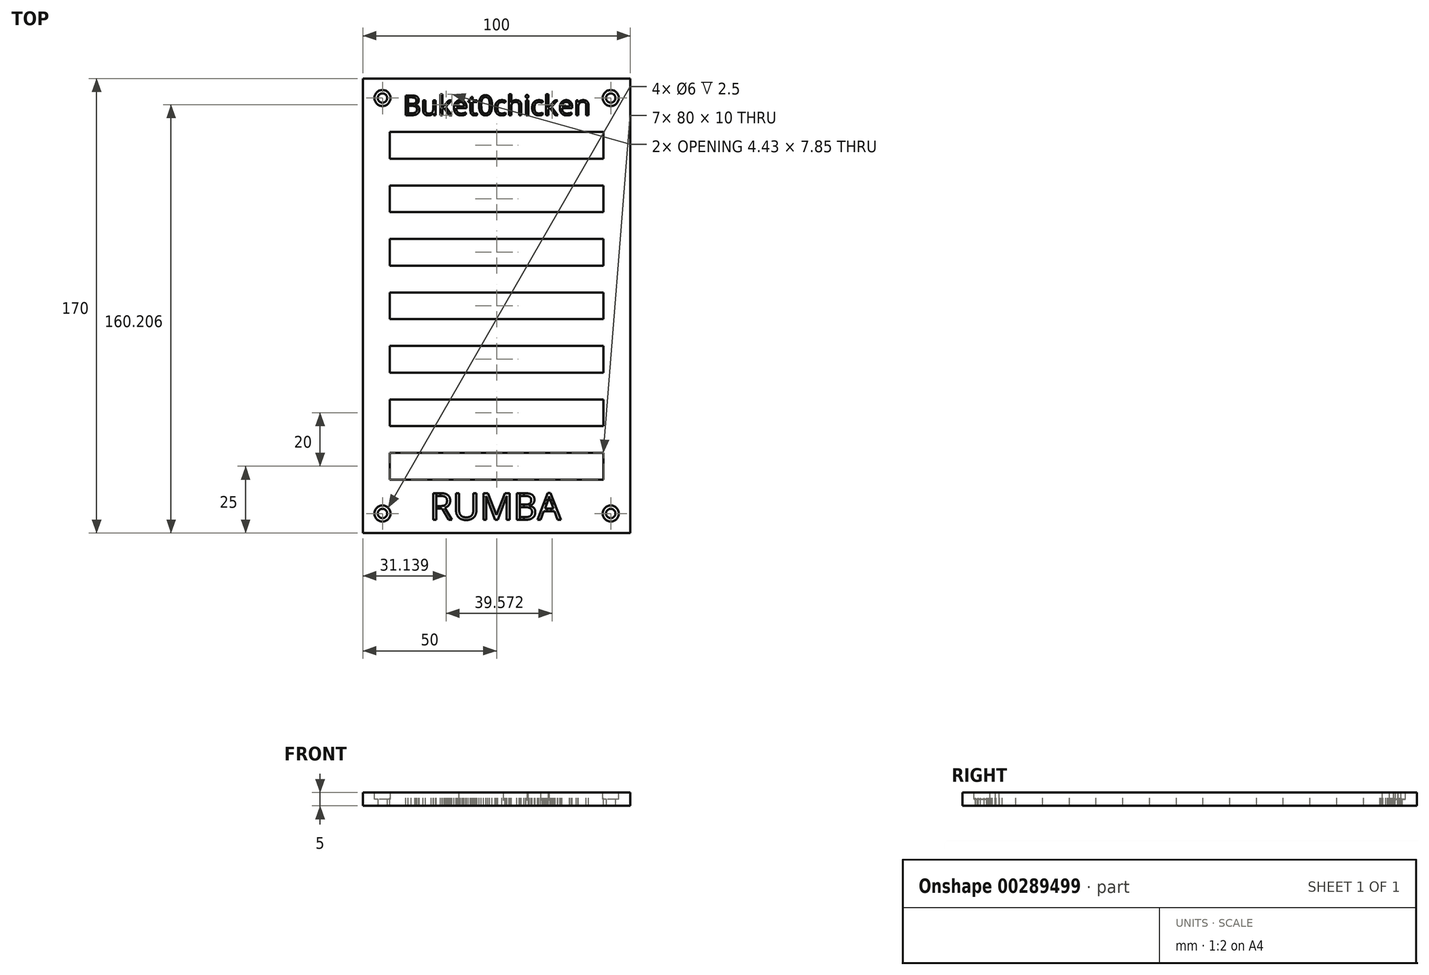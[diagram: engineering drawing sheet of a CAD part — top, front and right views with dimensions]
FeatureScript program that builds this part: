
annotation { "Feature Type Name" : "Feature", "Feature Type Description" : "" }
export const myFeature = defineFeature(function(context is Context, id is Id, definition is map)
    precondition{}
    {
        {
            var Q0;
            Q0=qCreatedBy(makeId("Top.planeOp"),FACE);
            var sketch = newSketch(context, id + "F0", { "sketchPlane" : qUnion([Q0])});
            skLineSegment(sketch, "E0.bottom", {"start": v(0, 0) * mm, "end": v(100, 0) * mm});
            skLineSegment(sketch, "E0.top", {"start": v(0, 170) * mm, "end": v(100, 170) * mm});
            skLineSegment(sketch, "E0.left", {"start": v(0, 0) * mm, "end": v(0, 170) * mm});
            skLineSegment(sketch, "E0.right", {"start": v(100, 0) * mm, "end": v(100, 170) * mm});
            skCircle(sketch, "E1", {"center": v(7.32, 162.68) * mm, "radius": 1.75 * mm});
            skCircle(sketch, "E2", {"center": v(92.68, 162.68) * mm, "radius": 1.75 * mm});
            skCircle(sketch, "E3", {"center": v(7.32, 7.32) * mm, "radius": 1.75 * mm});
            skCircle(sketch, "E4", {"center": v(92.68, 7.32) * mm, "radius": 1.75 * mm});
            skSolve(sketch);
        }
        {
            var Q0;
            Q0 = qSketchRegion(id + "F0", true);
            extrude(context, id + "F1", {"entities" : qUnion([Q0]), "depth" : 5 * mm});
        }
        {
            var Q0;
            Q0=makeQuery(id+"F1.opExtrude","CAP_FACE",FACE,{"disambiguationData":[OSD([sQuery(id+"F0.wireOp",EDGE,"E0.bottom"),sQuery(id+"F0.wireOp",EDGE,"E0.top"),sQuery(id+"F0.wireOp",EDGE,"E0.left"),sQuery(id+"F0.wireOp",EDGE,"E0.right"),sQuery(id+"F0.wireOp",EDGE,"E1"),sQuery(id+"F0.wireOp",EDGE,"E2"),sQuery(id+"F0.wireOp",EDGE,"E3"),sQuery(id+"F0.wireOp",EDGE,"E4")])],"isStart":false});
            var sketch = newSketch(context, id + "F2", { "sketchPlane" : qUnion([Q0])});
            skCircle(sketch, "E5.0", {"center": v(7.32, 162.68) * mm, "radius": 1.75 * mm, "construction": true});
            skCircle(sketch, "E6.0", {"center": v(92.68, 162.68) * mm, "radius": 1.75 * mm, "construction": true});
            skCircle(sketch, "E7.0", {"center": v(92.68, 7.32) * mm, "radius": 1.75 * mm, "construction": true});
            skCircle(sketch, "E8.0", {"center": v(7.32, 7.32) * mm, "radius": 1.75 * mm, "construction": true});
            skCircle(sketch, "E9", {"center": v(7.32, 162.68) * mm, "radius": 3 * mm});
            skCircle(sketch, "E10", {"center": v(92.68, 162.68) * mm, "radius": 3 * mm});
            skCircle(sketch, "E11", {"center": v(7.32, 7.32) * mm, "radius": 3 * mm});
            skCircle(sketch, "E12", {"center": v(92.68, 7.32) * mm, "radius": 3 * mm});
            skSolve(sketch);
        }
        {
            var Q0;
            Q0 = qSketchRegion(id + "F2", true);
            extrude(context, id + "F3", {"entities" : qUnion([Q0]), "operationType" : NewBodyOperationType.REMOVE, "oppositeDirection" : true, "depth" : 2.5 * mm});
        }
        {
            var Q0;
            Q0=makeQuery(id+"F1.opExtrude","CAP_FACE",FACE,{"disambiguationData":[OSD([sQuery(id+"F0.wireOp",EDGE,"E0.bottom"),sQuery(id+"F0.wireOp",EDGE,"E0.top"),sQuery(id+"F0.wireOp",EDGE,"E0.left"),sQuery(id+"F0.wireOp",EDGE,"E0.right"),sQuery(id+"F0.wireOp",EDGE,"E1"),sQuery(id+"F0.wireOp",EDGE,"E2"),sQuery(id+"F0.wireOp",EDGE,"E3"),sQuery(id+"F0.wireOp",EDGE,"E4")])],"isStart":false});
            var sketch = newSketch(context, id + "F4", { "sketchPlane" : qUnion([Q0])});
            skLineSegment(sketch, "E13.0.0", {"start": v(100, 170) * mm, "end": v(0, 170) * mm, "construction": true});
            skLineSegment(sketch, "E13.0.1", {"start": v(0, 170) * mm, "end": v(0, 0) * mm, "construction": true});
            skLineSegment(sketch, "E13.0.2", {"start": v(0, 0) * mm, "end": v(100, 0) * mm, "construction": true});
            skLineSegment(sketch, "E13.0.3", {"start": v(100, 0) * mm, "end": v(100, 170) * mm, "construction": true});
            skLineSegment(sketch, "E14.bottom", {"start": v(10, 150) * mm, "end": v(90, 150) * mm});
            skLineSegment(sketch, "E14.top", {"start": v(10, 140) * mm, "end": v(90, 140) * mm});
            skLineSegment(sketch, "E14.left", {"start": v(10, 150) * mm, "end": v(10, 140) * mm});
            skLineSegment(sketch, "E14.right", {"start": v(90, 150) * mm, "end": v(90, 140) * mm});
            skLineSegment(sketch, "E15.0.1.0", {"start": v(90, 130) * mm, "end": v(90, 120) * mm});
            skLineSegment(sketch, "E15.0.1.1", {"start": v(10, 130) * mm, "end": v(90, 130) * mm});
            skLineSegment(sketch, "E15.0.1.2", {"start": v(10, 120) * mm, "end": v(90, 120) * mm});
            skLineSegment(sketch, "E15.0.1.3", {"start": v(10, 130) * mm, "end": v(10, 120) * mm});
            skLineSegment(sketch, "E15.0.2.0", {"start": v(90, 110) * mm, "end": v(90, 100) * mm});
            skLineSegment(sketch, "E15.0.2.1", {"start": v(10, 110) * mm, "end": v(90, 110) * mm});
            skLineSegment(sketch, "E15.0.2.2", {"start": v(10, 100) * mm, "end": v(90, 100) * mm});
            skLineSegment(sketch, "E15.0.2.3", {"start": v(10, 110) * mm, "end": v(10, 100) * mm});
            skLineSegment(sketch, "E15.0.3.0", {"start": v(90, 90) * mm, "end": v(90, 80) * mm});
            skLineSegment(sketch, "E15.0.3.1", {"start": v(10, 90) * mm, "end": v(90, 90) * mm});
            skLineSegment(sketch, "E15.0.3.2", {"start": v(10, 80) * mm, "end": v(90, 80) * mm});
            skLineSegment(sketch, "E15.0.3.3", {"start": v(10, 90) * mm, "end": v(10, 80) * mm});
            skLineSegment(sketch, "E15.0.4.0", {"start": v(90, 70) * mm, "end": v(90, 60) * mm});
            skLineSegment(sketch, "E15.0.4.1", {"start": v(10, 70) * mm, "end": v(90, 70) * mm});
            skLineSegment(sketch, "E15.0.4.2", {"start": v(10, 60) * mm, "end": v(90, 60) * mm});
            skLineSegment(sketch, "E15.0.4.3", {"start": v(10, 70) * mm, "end": v(10, 60) * mm});
            skLineSegment(sketch, "E15.0.5.0", {"start": v(90, 50) * mm, "end": v(90, 40) * mm});
            skLineSegment(sketch, "E15.0.5.1", {"start": v(10, 50) * mm, "end": v(90, 50) * mm});
            skLineSegment(sketch, "E15.0.5.2", {"start": v(10, 40) * mm, "end": v(90, 40) * mm});
            skLineSegment(sketch, "E15.0.5.3", {"start": v(10, 50) * mm, "end": v(10, 40) * mm});
            skLineSegment(sketch, "E15.0.6.0", {"start": v(90, 30) * mm, "end": v(90, 20) * mm});
            skLineSegment(sketch, "E15.0.6.1", {"start": v(10, 30) * mm, "end": v(90, 30) * mm});
            skLineSegment(sketch, "E15.0.6.2", {"start": v(10, 20) * mm, "end": v(90, 20) * mm});
            skLineSegment(sketch, "E15.0.6.3", {"start": v(10, 30) * mm, "end": v(10, 20) * mm});
            skLineSegment(sketch, "E15.direction1", {"start": v(10, 140) * mm, "end": v(110.7, 140) * mm, "construction": true});
            skLineSegment(sketch, "E15.direction2", {"start": v(10, 140) * mm, "end": v(10, 120) * mm, "construction": true});
            skSolve(sketch);
        }
        {
            var Q0;
            Q0 = qSketchRegion(id + "F4", true);
            extrude(context, id + "F5", {"entities" : qUnion([Q0]), "operationType" : NewBodyOperationType.REMOVE, "endBound" : BoundingType.THROUGH_ALL, "oppositeDirection" : true, "depth" : 25 * mm});
        }
        {
            var Q0;
            Q0=makeQuery(id+"F1.opExtrude","CAP_FACE",FACE,{"disambiguationData":[OSD([sQuery(id+"F0.wireOp",EDGE,"E0.bottom"),sQuery(id+"F0.wireOp",EDGE,"E0.top"),sQuery(id+"F0.wireOp",EDGE,"E0.left"),sQuery(id+"F0.wireOp",EDGE,"E0.right"),sQuery(id+"F0.wireOp",EDGE,"E1"),sQuery(id+"F0.wireOp",EDGE,"E2"),sQuery(id+"F0.wireOp",EDGE,"E3"),sQuery(id+"F0.wireOp",EDGE,"E4")])],"isStart":false});
            var sketch = newSketch(context, id + "F6", { "sketchPlane" : qUnion([Q0])});
            skText(sketch, "E16", { "text": "Buket0chicken", "fontName": "OpenSans-Regular.ttf"});
            const initialGuessF6  = {"E16": [0.015, 0.15628, 1, 0, 0.00744]};
            skSetInitialGuess(sketch, initialGuessF6);
            skSolve(sketch);
        }
        {
            var Q0;
            Q0 = qSketchRegion(id + "F6", true);
            extrude(context, id + "F7", {"entities" : qUnion([Q0]), "operationType" : NewBodyOperationType.REMOVE, "endBound" : BoundingType.THROUGH_ALL, "oppositeDirection" : true, "depth" : 25 * mm});
        }
        {
            var Q0;
            {var subQ0=sQuery(id+"F0.wireOp",EDGE,"E0.right");var subQ1=sQuery(id+"F0.wireOp",EDGE,"E0.left");var subQ2=sQuery(id+"F0.wireOp",EDGE,"E0.top");var subQ3=sQuery(id+"F0.wireOp",EDGE,"E0.bottom");Q0=makeQuery(id+"F7.boolean.opBoolean","SPLIT",FACE,{"disambiguationData":[TD([makeQuery(id+"F1.opExtrude","SWEPT_FACE",FACE,{"disambiguationData":[OSD([subQ3])]})])],"derivedFrom":makeQuery(id+"F1.opExtrude","CAP_FACE",FACE,{"disambiguationData":[OSD([subQ3,subQ2,subQ1,subQ0,sQuery(id+"F0.wireOp",EDGE,"E1"),sQuery(id+"F0.wireOp",EDGE,"E2"),sQuery(id+"F0.wireOp",EDGE,"E3"),sQuery(id+"F0.wireOp",EDGE,"E4")])],"isStart":false})});}
            var sketch = newSketch(context, id + "F8", { "sketchPlane" : qUnion([Q0])});
            skText(sketch, "E17", { "text": "RUMBA", "fontName": "OpenSans-Regular.ttf"});
            const initialGuessF8  = {"E17": [0.025, 0.005, 1, 0, 0.01]};
            skSetInitialGuess(sketch, initialGuessF8);
            skSolve(sketch);
        }
        {
            var Q0;
            Q0 = qSketchRegion(id + "F8", true);
            extrude(context, id + "F9", {"entities" : qUnion([Q0]), "operationType" : NewBodyOperationType.REMOVE, "endBound" : BoundingType.THROUGH_ALL, "oppositeDirection" : true, "depth" : 25 * mm});
        }
        {
            var Q0;
            {var subQ114=sQuery(id+"F0.wireOp",EDGE,"E0.top");var subQ126=sQuery(id+"F0.wireOp",EDGE,"E0.left");var subQ134=sQuery(id+"F0.wireOp",EDGE,"E0.bottom");var subQ135=makeQuery(id+"F1.opExtrude","SWEPT_FACE",FACE,{"disambiguationData":[OSD([subQ134])]});var subQ142=sQuery(id+"F0.wireOp",EDGE,"E0.right");Q0=makeQuery(id+"F9.boolean.opBoolean","SPLIT",FACE,{"disambiguationData":[TD([subQ135])],"derivedFrom":makeQuery(id+"F7.boolean.opBoolean","SPLIT",FACE,{"disambiguationData":[TD([subQ135])],"derivedFrom":makeQuery(id+"F1.opExtrude","CAP_FACE",FACE,{"disambiguationData":[OSD([subQ134,subQ114,subQ126,subQ142,sQuery(id+"F0.wireOp",EDGE,"E1"),sQuery(id+"F0.wireOp",EDGE,"E2"),sQuery(id+"F0.wireOp",EDGE,"E3"),sQuery(id+"F0.wireOp",EDGE,"E4")])],"isStart":false})})});}
            var sketch = newSketch(context, id + "F10", { "sketchPlane" : qUnion([Q0])});
            skLineSegment(sketch, "E18.0.0", {"start": v(29.01, 13.9) * mm, "end": v(27.52, 13.9) * mm, "construction": true});
            skLineSegment(sketch, "E18.0.1", {"start": v(27.52, 13.9) * mm, "end": v(27.52, 10.11) * mm, "construction": true});
            skFitSpline(sketch, "E18.0.3", {"points": [v(29.1, 10.11) * mm, v(30.32, 10.11) * mm, v(30.89, 10.6) * mm], "construction": true});
            skFitSpline(sketch, "E18.0.4", {"points": [v(30.89, 10.6) * mm, v(31.46, 11.08) * mm, v(31.46, 12.05) * mm], "construction": true});
            skFitSpline(sketch, "E18.0.5", {"points": [v(31.46, 12.05) * mm, v(31.46, 13.04) * mm, v(30.88, 13.47) * mm], "construction": true});
            skFitSpline(sketch, "E18.0.6", {"points": [v(30.88, 13.47) * mm, v(30.3, 13.9) * mm, v(29.01, 13.9) * mm], "construction": true});
            skLineSegment(sketch, "E19.0", {"start": v(26.36, 14.92) * mm, "end": v(29.08, 14.92) * mm, "construction": true});
            skFitSpline(sketch, "E20.0", {"points": [v(29.08, 14.92) * mm, v(30.9, 14.92) * mm, v(31.78, 14.22) * mm], "construction": true});
            skLineSegment(sketch, "E21.0", {"start": v(29.59, 9.12) * mm, "end": v(27.52, 9.12) * mm, "construction": true});
            skLineSegment(sketch, "E22.0.0", {"start": v(60.45, 13.92) * mm, "end": v(58.75, 13.92) * mm, "construction": true});
            skLineSegment(sketch, "E22.0.1", {"start": v(58.75, 13.92) * mm, "end": v(58.75, 10.67) * mm, "construction": true});
            skLineSegment(sketch, "E22.0.2", {"start": v(58.75, 10.67) * mm, "end": v(60.65, 10.67) * mm, "construction": true});
            skFitSpline(sketch, "E22.0.3", {"points": [v(60.65, 10.67) * mm, v(61.87, 10.67) * mm, v(62.4, 11.05) * mm], "construction": true});
            skFitSpline(sketch, "E22.0.4", {"points": [v(62.4, 11.05) * mm, v(62.94, 11.44) * mm, v(62.94, 12.34) * mm], "construction": true});
            skFitSpline(sketch, "E22.0.5", {"points": [v(62.94, 12.34) * mm, v(62.94, 13.18) * mm, v(62.35, 13.55) * mm], "construction": true});
            skFitSpline(sketch, "E22.0.6", {"points": [v(62.35, 13.55) * mm, v(61.75, 13.92) * mm, v(60.45, 13.92) * mm], "construction": true});
            skLineSegment(sketch, "E23.0", {"start": v(57.6, 14.92) * mm, "end": v(60.4, 14.92) * mm, "construction": true});
            skFitSpline(sketch, "E24.0", {"points": [v(60.4, 14.92) * mm, v(62.37, 14.92) * mm, v(63.25, 14.33) * mm], "construction": true});
            skFitSpline(sketch, "E25.0.0", {"points": [v(62.61, 9.26) * mm, v(62, 9.7) * mm, v(60.72, 9.7) * mm], "construction": true});
            skLineSegment(sketch, "E25.0.1", {"start": v(60.72, 9.7) * mm, "end": v(58.75, 9.7) * mm, "construction": true});
            skLineSegment(sketch, "E25.0.2", {"start": v(58.75, 9.7) * mm, "end": v(58.75, 5.98) * mm, "construction": true});
            skLineSegment(sketch, "E25.0.3", {"start": v(58.75, 5.98) * mm, "end": v(60.82, 5.98) * mm, "construction": true});
            skFitSpline(sketch, "E25.0.4", {"points": [v(60.82, 5.98) * mm, v(62.02, 5.98) * mm, v(62.63, 6.45) * mm], "construction": true});
            skFitSpline(sketch, "E25.0.5", {"points": [v(62.63, 6.45) * mm, v(63.23, 6.91) * mm, v(63.23, 7.9) * mm], "construction": true});
            skFitSpline(sketch, "E25.0.6", {"points": [v(63.23, 7.9) * mm, v(63.23, 8.83) * mm, v(62.61, 9.26) * mm], "construction": true});
            skLineSegment(sketch, "E26.0", {"start": v(61.06, 5) * mm, "end": v(57.6, 5) * mm, "construction": true});
            skLineSegment(sketch, "E27.0.0", {"start": v(69.2, 12.26) * mm, "end": v(68.03, 9.2) * mm, "construction": true});
            skLineSegment(sketch, "E27.0.1", {"start": v(68.03, 9.2) * mm, "end": v(71.24, 9.2) * mm, "construction": true});
            skLineSegment(sketch, "E27.0.2", {"start": v(71.24, 9.2) * mm, "end": v(70.08, 12.26) * mm, "construction": true});
            skFitSpline(sketch, "E27.0.3", {"points": [v(70.08, 12.26) * mm, v(69.86, 12.85) * mm, v(69.62, 13.7) * mm], "construction": true});
            skFitSpline(sketch, "E27.0.4", {"points": [v(69.62, 13.7) * mm, v(69.47, 13.04) * mm, v(69.2, 12.26) * mm], "construction": true});
            skLineSegment(sketch, "E28.0.0", {"start": v(100, 170) * mm, "end": v(0, 170) * mm, "construction": true});
            skLineSegment(sketch, "E28.0.1", {"start": v(0, 170) * mm, "end": v(0, 0) * mm, "construction": true});
            skLineSegment(sketch, "E28.0.2", {"start": v(0, 0) * mm, "end": v(100, 0) * mm, "construction": true});
            skLineSegment(sketch, "E28.0.3", {"start": v(100, 0) * mm, "end": v(100, 170) * mm, "construction": true});
            skLineSegment(sketch, "E29.0", {"start": v(70.12, 14.96) * mm, "end": v(74.02, 5) * mm, "construction": true});
            skLineSegment(sketch, "E30.0", {"start": v(65.23, 5) * mm, "end": v(69.15, 14.96) * mm, "construction": true});
            skLineSegment(sketch, "E31.0", {"start": v(71.6, 8.15) * mm, "end": v(67.62, 8.15) * mm, "construction": true});
            skLineSegment(sketch, "E32.0.0", {"start": v(18.13, 162.91) * mm, "end": v(16.87, 162.91) * mm, "construction": true});
            skLineSegment(sketch, "E32.0.1", {"start": v(16.87, 162.91) * mm, "end": v(16.87, 160.5) * mm, "construction": true});
            skLineSegment(sketch, "E32.0.2", {"start": v(16.87, 160.5) * mm, "end": v(18.28, 160.5) * mm, "construction": true});
            skFitSpline(sketch, "E32.0.3", {"points": [v(18.28, 160.5) * mm, v(19.2, 160.5) * mm, v(19.6, 160.78) * mm], "construction": true});
            skFitSpline(sketch, "E32.0.4", {"points": [v(19.6, 160.78) * mm, v(19.99, 161.07) * mm, v(19.99, 161.74) * mm], "construction": true});
            skFitSpline(sketch, "E32.0.5", {"points": [v(19.99, 161.74) * mm, v(19.99, 162.36) * mm, v(19.55, 162.64) * mm], "construction": true});
            skFitSpline(sketch, "E32.0.6", {"points": [v(19.55, 162.64) * mm, v(19.1, 162.91) * mm, v(18.13, 162.91) * mm], "construction": true});
            skFitSpline(sketch, "E33.0.0", {"points": [v(19.74, 159.45) * mm, v(19.28, 159.77) * mm, v(18.34, 159.77) * mm], "construction": true});
            skLineSegment(sketch, "E33.0.1", {"start": v(18.34, 159.77) * mm, "end": v(16.87, 159.77) * mm, "construction": true});
            skLineSegment(sketch, "E33.0.2", {"start": v(16.87, 159.77) * mm, "end": v(16.87, 157.01) * mm, "construction": true});
            skLineSegment(sketch, "E33.0.3", {"start": v(16.87, 157.01) * mm, "end": v(18.41, 157.01) * mm, "construction": true});
            skFitSpline(sketch, "E33.0.4", {"points": [v(18.41, 157.01) * mm, v(19.3, 157.01) * mm, v(19.75, 157.36) * mm], "construction": true});
            skFitSpline(sketch, "E33.0.5", {"points": [v(19.75, 157.36) * mm, v(20.2, 157.7) * mm, v(20.2, 158.44) * mm], "construction": true});
            skFitSpline(sketch, "E33.0.6", {"points": [v(20.2, 158.44) * mm, v(20.2, 159.13) * mm, v(19.74, 159.45) * mm], "construction": true});
            skLineSegment(sketch, "E34.0", {"start": v(18.59, 156.28) * mm, "end": v(16.01, 156.28) * mm, "construction": true});
            skLineSegment(sketch, "E35.0", {"start": v(16.01, 163.66) * mm, "end": v(18.1, 163.66) * mm, "construction": true});
            skFitSpline(sketch, "E36.0.0", {"points": [v(37.82, 159.58) * mm, v(37.82, 160.37) * mm, v(37.46, 160.79) * mm], "construction": true});
            skFitSpline(sketch, "E36.0.1", {"points": [v(37.46, 160.79) * mm, v(37.11, 161.2) * mm, v(36.45, 161.2) * mm]});
            skFitSpline(sketch, "E36.0.2", {"points": [v(36.45, 161.2) * mm, v(35.79, 161.2) * mm, v(35.4, 160.78) * mm]});
            skFitSpline(sketch, "E36.0.3", {"points": [v(35.4, 160.78) * mm, v(35, 160.34) * mm, v(34.93, 159.58) * mm], "construction": true});
            skLineSegment(sketch, "E36.0.4", {"start": v(34.93, 159.58) * mm, "end": v(37.82, 159.58) * mm, "construction": true});
            skFitSpline(sketch, "E37.0", {"points": [v(36.47, 161.91) * mm, v(37.5, 161.91) * mm, v(38.1, 161.23) * mm]});
            skFitSpline(sketch, "E38.0", {"points": [v(34.7, 161.12) * mm, v(35.35, 161.91) * mm, v(36.47, 161.91) * mm], "construction": true});
            skLineSegment(sketch, "E39.0", {"start": v(38.71, 158.9) * mm, "end": v(34.9, 158.9) * mm, "construction": true});
            skPoint(sketch, "E40.0", {"position": v(47.44, 159.98) * mm});
            skFitSpline(sketch, "E41.0.0", {"points": [v(45.85, 163.05) * mm, v(45.02, 163.05) * mm, v(44.64, 162.32) * mm]});
            skFitSpline(sketch, "E41.0.1", {"points": [v(44.64, 162.32) * mm, v(44.26, 161.59) * mm, v(44.26, 159.98) * mm], "construction": true});
            skFitSpline(sketch, "E41.0.2", {"points": [v(44.26, 159.98) * mm, v(44.26, 158.37) * mm, v(44.64, 157.64) * mm], "construction": true});
            skFitSpline(sketch, "E41.0.3", {"points": [v(44.64, 157.64) * mm, v(45.02, 156.9) * mm, v(45.85, 156.9) * mm]});
            skFitSpline(sketch, "E41.0.4", {"points": [v(45.85, 156.9) * mm, v(46.69, 156.9) * mm, v(47.06, 157.64) * mm]});
            skFitSpline(sketch, "E41.0.5", {"points": [v(47.06, 157.64) * mm, v(47.44, 158.39) * mm, v(47.44, 159.98) * mm], "construction": true});
            skFitSpline(sketch, "E41.0.6", {"points": [v(47.44, 159.98) * mm, v(47.44, 161.57) * mm, v(47.06, 162.3) * mm], "construction": true});
            skFitSpline(sketch, "E41.0.7", {"points": [v(47.06, 162.3) * mm, v(46.69, 163.05) * mm, v(45.85, 163.05) * mm]});
            skFitSpline(sketch, "E42.0", {"points": [v(45.85, 163.77) * mm, v(47.05, 163.77) * mm, v(47.67, 162.8) * mm]});
            skFitSpline(sketch, "E43.0", {"points": [v(44.02, 162.84) * mm, v(44.62, 163.77) * mm, v(45.85, 163.77) * mm]});
            skPoint(sketch, "E44.0", {"position": v(44.81, 156.42) * mm});
            skFitSpline(sketch, "E45.0", {"points": [v(45.85, 156.18) * mm, v(44.66, 156.18) * mm, v(44.04, 157.15) * mm]});
            skFitSpline(sketch, "E46.0", {"points": [v(47.7, 157.12) * mm, v(47.09, 156.18) * mm, v(45.85, 156.18) * mm]});
            skFitSpline(sketch, "E47.0.0", {"points": [v(77.38, 159.58) * mm, v(77.38, 160.37) * mm, v(77.03, 160.79) * mm], "construction": true});
            skFitSpline(sketch, "E47.0.1", {"points": [v(77.03, 160.79) * mm, v(76.68, 161.2) * mm, v(76.02, 161.2) * mm], "construction": true});
            skFitSpline(sketch, "E47.0.2", {"points": [v(76.02, 161.2) * mm, v(75.35, 161.2) * mm, v(74.96, 160.78) * mm], "construction": true});
            skFitSpline(sketch, "E47.0.3", {"points": [v(74.96, 160.78) * mm, v(74.56, 160.34) * mm, v(74.5, 159.58) * mm], "construction": true});
            skLineSegment(sketch, "E47.0.4", {"start": v(74.5, 159.58) * mm, "end": v(77.38, 159.58) * mm, "construction": true});
            skFitSpline(sketch, "E48.0", {"points": [v(76.03, 161.91) * mm, v(77.07, 161.91) * mm, v(77.67, 161.23) * mm], "construction": true});
            skFitSpline(sketch, "E49.0", {"points": [v(74.26, 161.12) * mm, v(74.92, 161.91) * mm, v(76.03, 161.91) * mm], "construction": true});
            skLineSegment(sketch, "E50.0", {"start": v(78.28, 158.9) * mm, "end": v(74.47, 158.9) * mm, "construction": true});
            skLineSegment(sketch, "E51.bottom", {"start": v(16.87, 162.91) * mm, "end": v(18.1, 162.91) * mm});
            skLineSegment(sketch, "E51.top", {"start": v(16.87, 163.66) * mm, "end": v(18.1, 163.66) * mm});
            skLineSegment(sketch, "E51.left", {"start": v(16.87, 162.91) * mm, "end": v(16.87, 163.66) * mm});
            skLineSegment(sketch, "E51.right", {"start": v(18.1, 162.91) * mm, "end": v(18.1, 163.66) * mm});
            skLineSegment(sketch, "E52.bottom", {"start": v(16.87, 160.5) * mm, "end": v(18.1, 160.5) * mm});
            skLineSegment(sketch, "E52.top", {"start": v(16.87, 159.77) * mm, "end": v(18.1, 159.77) * mm});
            skLineSegment(sketch, "E52.left", {"start": v(16.87, 160.5) * mm, "end": v(16.87, 159.77) * mm});
            skLineSegment(sketch, "E52.right", {"start": v(18.1, 160.5) * mm, "end": v(18.1, 159.77) * mm});
            skLineSegment(sketch, "E53.bottom", {"start": v(16.87, 157.01) * mm, "end": v(18.1, 157.01) * mm});
            skLineSegment(sketch, "E53.top", {"start": v(16.87, 156.28) * mm, "end": v(18.1, 156.28) * mm});
            skLineSegment(sketch, "E53.left", {"start": v(16.87, 157.01) * mm, "end": v(16.87, 156.28) * mm});
            skLineSegment(sketch, "E53.right", {"start": v(18.1, 157.01) * mm, "end": v(18.1, 156.28) * mm});
            skLineSegment(sketch, "E54", {"start": v(35.85, 161.1) * mm, "end": v(35.85, 161.84) * mm});
            skLineSegment(sketch, "E55", {"start": v(37.08, 161.08) * mm, "end": v(37.08, 161.1) * mm});
            skLineSegment(sketch, "E56.bottom", {"start": v(35.85, 159.58) * mm, "end": v(37.08, 159.58) * mm});
            skLineSegment(sketch, "E56.top", {"start": v(35.85, 158.9) * mm, "end": v(37.08, 158.9) * mm});
            skLineSegment(sketch, "E56.left", {"start": v(35.85, 159.58) * mm, "end": v(35.85, 158.9) * mm});
            skLineSegment(sketch, "E56.right", {"start": v(37.08, 159.58) * mm, "end": v(37.08, 158.9) * mm});
            skLineSegment(sketch, "E57", {"start": v(45.23, 163.7) * mm, "end": v(45.23, 162.92) * mm});
            skLineSegment(sketch, "E58", {"start": v(46.46, 163.7) * mm, "end": v(46.46, 162.92) * mm});
            skLineSegment(sketch, "E59", {"start": v(45.23, 157.03) * mm, "end": v(45.23, 156.25) * mm});
            skLineSegment(sketch, "E60", {"start": v(46.46, 157.03) * mm, "end": v(46.46, 156.25) * mm});
            skPoint(sketch, "E61.orphan", {"position": v(47.7, 157.12) * mm});
            skPoint(sketch, "E62.orphan", {"position": v(44.04, 157.15) * mm});
            skPoint(sketch, "E63.orphan", {"position": v(47.67, 162.8) * mm});
            skPoint(sketch, "E64.orphan", {"position": v(44.02, 162.84) * mm});
            skFitSpline(sketch, "E65", {"points": [v(34.7, 161.12) * mm, v(35.35, 161.91) * mm, v(36.47, 161.91) * mm]});
            skFitSpline(sketch, "E66", {"points": [v(36.47, 161.91) * mm, v(37.5, 161.91) * mm, v(38.1, 161.23) * mm], "construction": true});
            skFitSpline(sketch, "E67", {"points": [v(36.45, 161.2) * mm, v(35.79, 161.2) * mm, v(35.4, 160.78) * mm, v(36.45, 161.2) * mm]});
            skLineSegment(sketch, "E68", {"start": v(37.08, 161.1) * mm, "end": v(37.08, 161.84) * mm});
            skFitSpline(sketch, "E69", {"points": [v(36.45, 161.2) * mm, v(35.79, 161.2) * mm, v(35.4, 160.78) * mm], "construction": true});
            skLineSegment(sketch, "E70.bottom", {"start": v(27.52, 13.9) * mm, "end": v(29.01, 13.9) * mm});
            skLineSegment(sketch, "E70.top", {"start": v(27.52, 14.92) * mm, "end": v(29.01, 14.92) * mm});
            skLineSegment(sketch, "E70.left", {"start": v(27.52, 13.9) * mm, "end": v(27.52, 14.92) * mm});
            skLineSegment(sketch, "E70.right", {"start": v(29.01, 13.9) * mm, "end": v(29.01, 14.92) * mm});
            skLineSegment(sketch, "E71.bottom", {"start": v(27.52, 9.12) * mm, "end": v(29.01, 9.12) * mm});
            skLineSegment(sketch, "E71.top", {"start": v(27.52, 10.11) * mm, "end": v(29.01, 10.11) * mm});
            skLineSegment(sketch, "E71.left", {"start": v(27.52, 9.12) * mm, "end": v(27.52, 10.11) * mm});
            skLineSegment(sketch, "E71.right", {"start": v(29.01, 9.12) * mm, "end": v(29.01, 10.11) * mm});
            skLineSegment(sketch, "E72.bottom", {"start": v(58.75, 13.92) * mm, "end": v(60.25, 13.92) * mm});
            skLineSegment(sketch, "E72.top", {"start": v(58.75, 14.92) * mm, "end": v(60.25, 14.92) * mm});
            skLineSegment(sketch, "E72.left", {"start": v(58.75, 13.92) * mm, "end": v(58.75, 14.92) * mm});
            skLineSegment(sketch, "E72.right", {"start": v(60.25, 13.92) * mm, "end": v(60.25, 14.92) * mm});
            skLineSegment(sketch, "E73.bottom", {"start": v(58.75, 10.67) * mm, "end": v(60.25, 10.67) * mm});
            skLineSegment(sketch, "E73.top", {"start": v(58.75, 9.7) * mm, "end": v(60.25, 9.7) * mm});
            skLineSegment(sketch, "E73.left", {"start": v(58.75, 10.67) * mm, "end": v(58.75, 9.7) * mm});
            skLineSegment(sketch, "E73.right", {"start": v(60.25, 10.67) * mm, "end": v(60.25, 9.7) * mm});
            skLineSegment(sketch, "E74.bottom", {"start": v(58.75, 5.98) * mm, "end": v(60.25, 5.98) * mm});
            skLineSegment(sketch, "E74.top", {"start": v(58.75, 5) * mm, "end": v(60.25, 5) * mm});
            skLineSegment(sketch, "E74.left", {"start": v(58.75, 5.98) * mm, "end": v(58.75, 5) * mm});
            skLineSegment(sketch, "E74.right", {"start": v(60.25, 5.98) * mm, "end": v(60.25, 5) * mm});
            skLineSegment(sketch, "E75.bottom", {"start": v(68.87, 9.2) * mm, "end": v(70.37, 9.2) * mm});
            skLineSegment(sketch, "E75.top", {"start": v(68.87, 8.15) * mm, "end": v(70.37, 8.15) * mm});
            skLineSegment(sketch, "E75.left", {"start": v(68.87, 9.2) * mm, "end": v(68.87, 8.15) * mm});
            skLineSegment(sketch, "E75.right", {"start": v(70.37, 9.2) * mm, "end": v(70.37, 8.15) * mm});
            skLineSegment(sketch, "E76", {"start": v(70.08, 12.26) * mm, "end": v(71.03, 12.64) * mm});
            skLineSegment(sketch, "E77", {"start": v(71.03, 12.64) * mm, "end": v(71.58, 11.24) * mm});
            skLineSegment(sketch, "E78", {"start": v(71.58, 11.24) * mm, "end": v(70.61, 10.86) * mm});
            skLineSegment(sketch, "E79", {"start": v(70.61, 10.86) * mm, "end": v(70.08, 12.26) * mm});
            skLineSegment(sketch, "E80", {"start": v(69.62, 13.7) * mm, "end": v(69.63, 9.2) * mm, "construction": true});
            skLineSegment(sketch, "E81.MirrorCS", {"start": v(68.65, 10.85) * mm, "end": v(69.17, 12.26) * mm});
            skLineSegment(sketch, "E82.MirrorCS", {"start": v(67.68, 11.23) * mm, "end": v(68.65, 10.85) * mm});
            skLineSegment(sketch, "E83.MirrorCS", {"start": v(69.17, 12.26) * mm, "end": v(68.22, 12.63) * mm});
            skLineSegment(sketch, "E84.MirrorCS", {"start": v(68.22, 12.63) * mm, "end": v(67.68, 11.23) * mm});
            skSolve(sketch);
        }
        {
            var Q0;
            Q0 = qSketchRegion(id + "F10", true);
            var Q1;
            {var subQ114=sQuery(id+"F0.wireOp",EDGE,"E0.top");var subQ119=sQuery(id+"F0.wireOp",EDGE,"E4");var subQ126=sQuery(id+"F0.wireOp",EDGE,"E3");var subQ135=sQuery(id+"F0.wireOp",EDGE,"E2");var subQ141=sQuery(id+"F0.wireOp",EDGE,"E1");var subQ149=sQuery(id+"F0.wireOp",EDGE,"E0.left");var subQ153=sQuery(id+"F0.wireOp",EDGE,"E0.bottom");var subQ154=makeQuery(id+"F1.opExtrude","SWEPT_FACE",FACE,{"disambiguationData":[OSD([subQ153])]});var subQ157=sQuery(id+"F0.wireOp",EDGE,"E0.right");Q1=makeQuery(id+"F9.boolean.opBoolean","SPLIT",FACE,{"disambiguationData":[TD([subQ154])],"derivedFrom":makeQuery(id+"F7.boolean.opBoolean","SPLIT",FACE,{"disambiguationData":[TD([subQ154])],"derivedFrom":makeQuery(id+"F1.opExtrude","CAP_FACE",FACE,{"disambiguationData":[OSD([subQ153,subQ114,subQ149,subQ157,subQ141,subQ135,subQ126,subQ119])],"isStart":true})})});}
            extrude(context, id + "F11", {"entities" : qUnion([Q0]), "endBound" : BoundingType.UP_TO_SURFACE, "oppositeDirection" : true, "endBoundEntityFace" : qUnion([Q1]), "depth" : 25 * mm});
        }
    });
